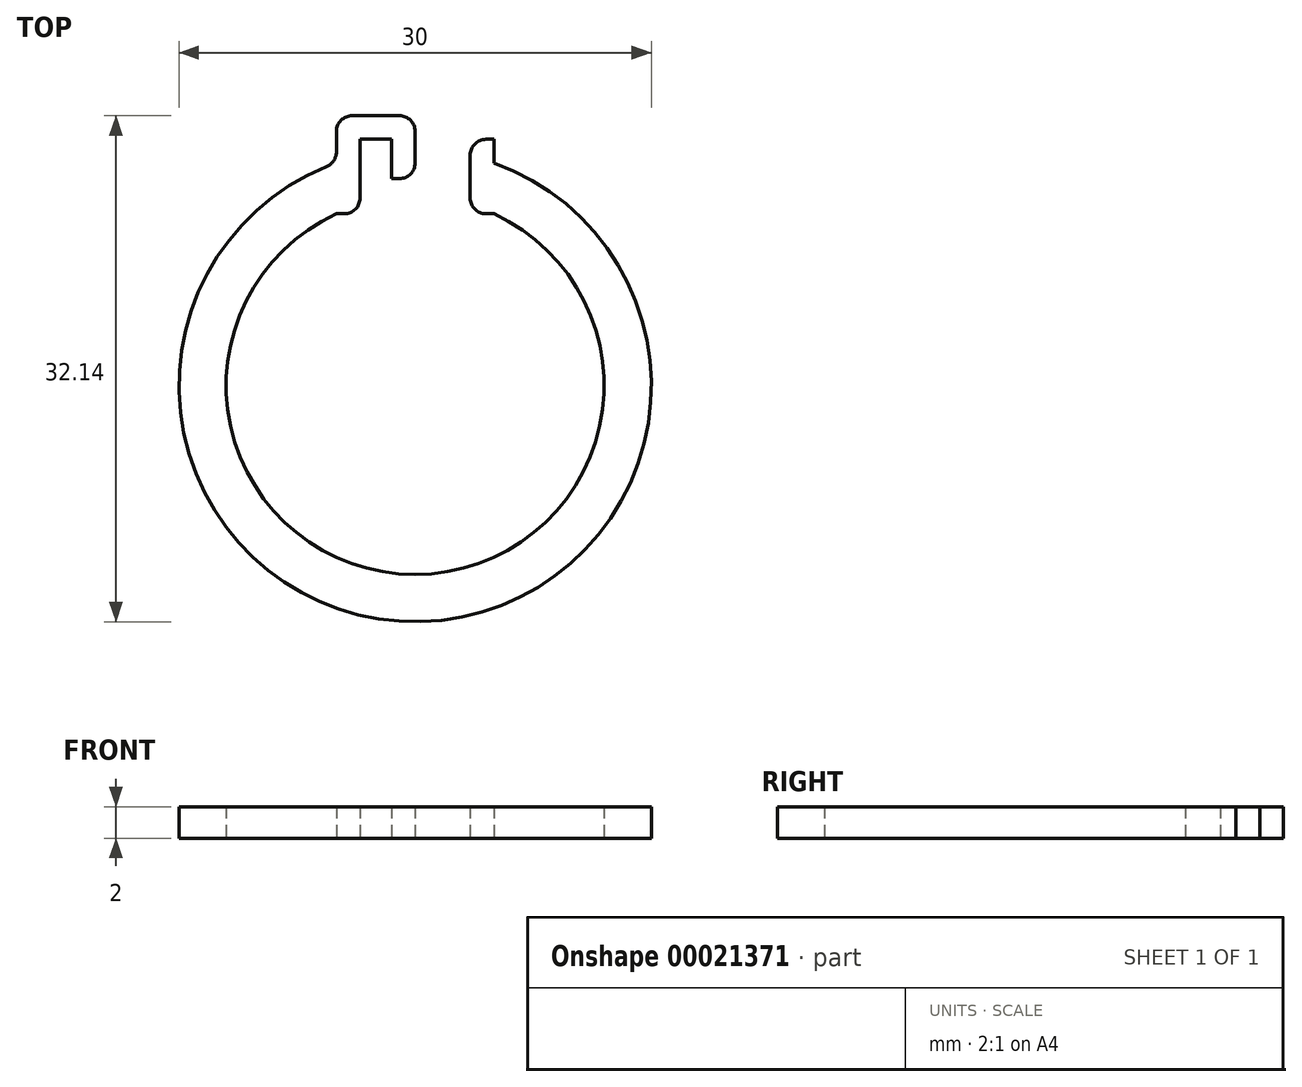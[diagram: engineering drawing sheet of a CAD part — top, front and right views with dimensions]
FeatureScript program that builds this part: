
annotation { "Feature Type Name" : "Feature", "Feature Type Description" : "" }
export const myFeature = defineFeature(function(context is Context, id is Id, definition is map)
    precondition{}
    {
        {
            var Q0;
            Q0=qCreatedBy(makeId("Top.planeOp"),FACE);
            var sketch = newSketch(context, id + "F0", { "sketchPlane" : qUnion([Q0])});
            skArc(sketch, "E0", {"start": v(-5.63, 13.9) * mm, "mid": v(0.33, -15) * mm, "end": v(5, 14.14) * mm});
            skArc(sketch, "E1", {"start": v(-5, 10.9) * mm, "mid": v(0, -12) * mm, "end": v(5, 10.9) * mm});
            skLineSegment(sketch, "E2", {"start": v(-5, 10.9) * mm, "end": v(-5, 14.14) * mm, "construction": true});
            skLineSegment(sketch, "E3", {"start": v(5, 14.14) * mm, "end": v(5, 10.9) * mm, "construction": true});
            skLineSegment(sketch, "E4", {"start": v(5, 10.9) * mm, "end": v(4.5, 10.9) * mm});
            skLineSegment(sketch, "E5", {"start": v(3.5, 11.9) * mm, "end": v(3.5, 14.64) * mm});
            skLineSegment(sketch, "E6", {"start": v(4.5, 15.64) * mm, "end": v(5, 15.64) * mm});
            skLineSegment(sketch, "E7", {"start": v(5, 15.64) * mm, "end": v(5, 14.14) * mm});
            skLineSegment(sketch, "E8", {"start": v(-5, 14.83) * mm, "end": v(-5, 16.14) * mm});
            skLineSegment(sketch, "E9", {"start": v(-4, 17.14) * mm, "end": v(-1, 17.14) * mm});
            skLineSegment(sketch, "E10", {"start": v(0, 16.14) * mm, "end": v(0, 14.14) * mm});
            skLineSegment(sketch, "E11", {"start": v(-1, 13.14) * mm, "end": v(-1.5, 13.14) * mm});
            skLineSegment(sketch, "E12", {"start": v(-1.5, 13.14) * mm, "end": v(-1.5, 15.64) * mm});
            skLineSegment(sketch, "E13", {"start": v(-1.5, 15.64) * mm, "end": v(-3.5, 15.64) * mm});
            skLineSegment(sketch, "E14", {"start": v(-3.5, 15.64) * mm, "end": v(-3.5, 11.9) * mm});
            skLineSegment(sketch, "E15", {"start": v(-4.5, 10.9) * mm, "end": v(-5, 10.9) * mm});
            skPoint(sketch, "E16.visualSharp", {"position": v(3.5, 15.64) * mm});
            skArc(sketch, "E16.filletArc", {"start": v(4.5, 15.64) * mm, "mid": v(3.8, 15.35) * mm, "end": v(3.5, 14.64) * mm});
            skPoint(sketch, "E17.visualSharp", {"position": v(-3.5, 10.9) * mm});
            skArc(sketch, "E17.filletArc", {"start": v(-4.5, 10.9) * mm, "mid": v(-3.8, 11.2) * mm, "end": v(-3.5, 11.9) * mm});
            skPoint(sketch, "E18.visualSharp", {"position": v(-5, 14.14) * mm});
            skArc(sketch, "E18.filletArc", {"start": v(-5.63, 13.9) * mm, "mid": v(-5.17, 14.27) * mm, "end": v(-5, 14.83) * mm});
            skPoint(sketch, "E19.visualSharp", {"position": v(-5, 17.14) * mm});
            skArc(sketch, "E19.filletArc", {"start": v(-4, 17.14) * mm, "mid": v(-4.7, 16.85) * mm, "end": v(-5, 16.14) * mm});
            skPoint(sketch, "E20.visualSharp", {"position": v(0, 13.14) * mm});
            skArc(sketch, "E20.filletArc", {"start": v(-1, 13.14) * mm, "mid": v(-0.3, 13.44) * mm, "end": v(0, 14.14) * mm});
            skPoint(sketch, "E21.visualSharp", {"position": v(0, 17.14) * mm});
            skArc(sketch, "E21.filletArc", {"start": v(0, 16.14) * mm, "mid": v(-0.3, 16.85) * mm, "end": v(-1, 17.14) * mm});
            skPoint(sketch, "E22.visualSharp", {"position": v(3.5, 10.9) * mm});
            skArc(sketch, "E22.filletArc", {"start": v(3.5, 11.9) * mm, "mid": v(3.8, 11.2) * mm, "end": v(4.5, 10.9) * mm});
            skSolve(sketch);
        }
        {
            var Q0;
            Q0 = qSketchRegion(id + "F0", true);
            extrude(context, id + "F1", {"entities" : qUnion([Q0]), "depth" : 2 * mm});
        }
    });
